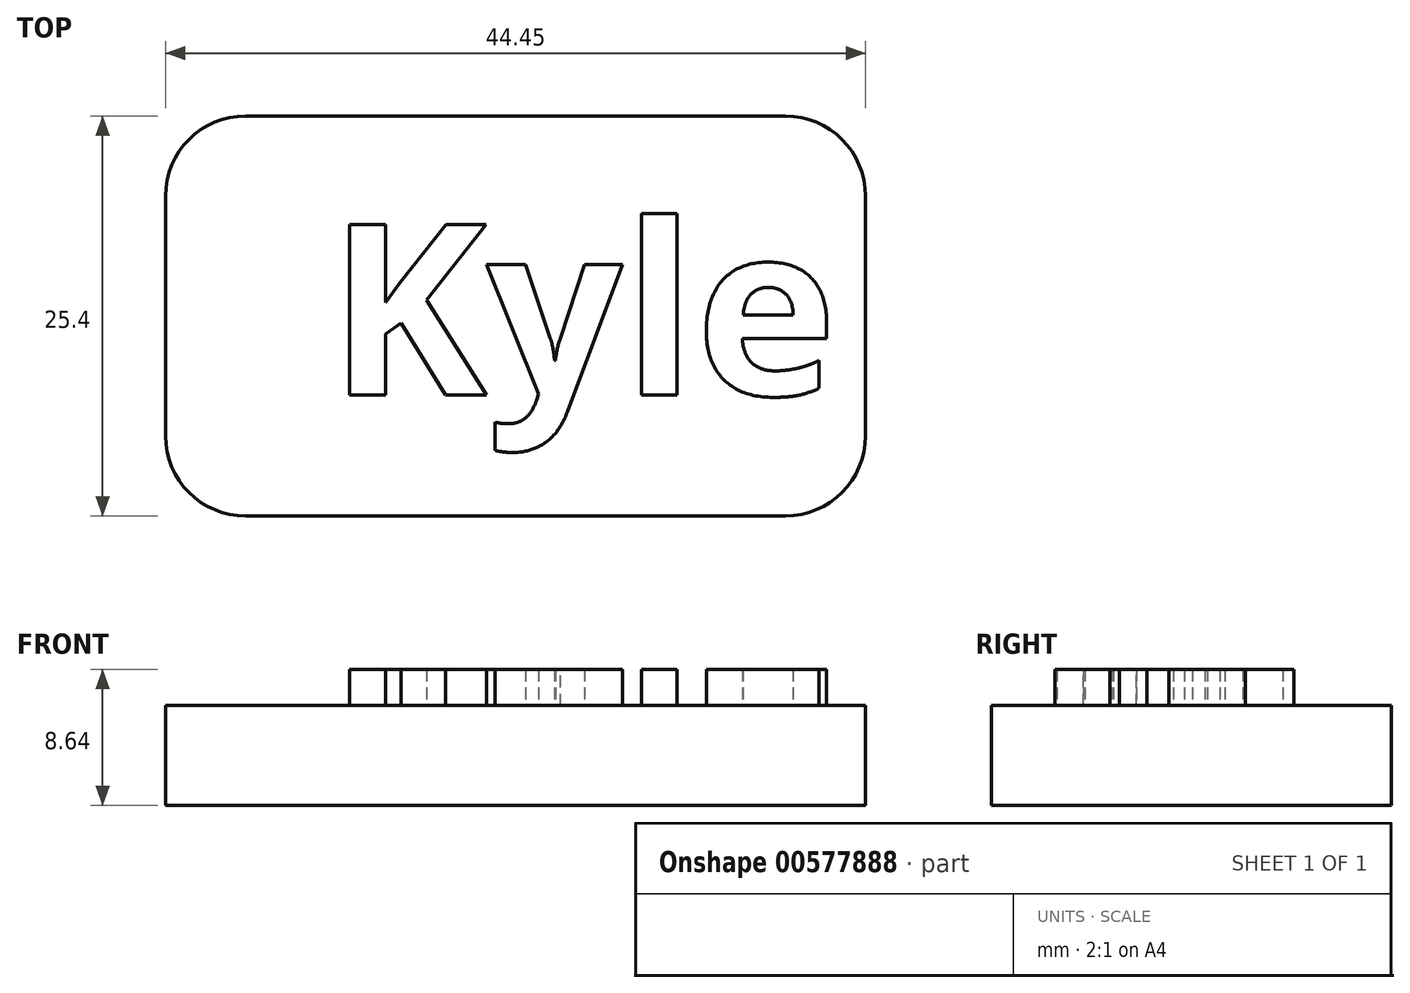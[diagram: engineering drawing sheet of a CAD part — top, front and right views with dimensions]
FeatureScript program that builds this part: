
annotation { "Feature Type Name" : "Feature", "Feature Type Description" : "" }
export const myFeature = defineFeature(function(context is Context, id is Id, definition is map)
    precondition{}
    {
        {
            var Q0;
            Q0=qCreatedBy(makeId("Top.planeOp"),FACE);
            var sketch = newSketch(context, id + "F0", { "sketchPlane" : qUnion([Q0])});
            skLineSegment(sketch, "E0.bottom", {"start": v(-63.11, 52.38) * mm, "end": v(-18.66, 52.38) * mm});
            skLineSegment(sketch, "E0.top", {"start": v(-63.11, 26.98) * mm, "end": v(-18.66, 26.98) * mm});
            skLineSegment(sketch, "E0.left", {"start": v(-63.11, 52.38) * mm, "end": v(-63.11, 26.98) * mm});
            skLineSegment(sketch, "E0.right", {"start": v(-18.66, 52.38) * mm, "end": v(-18.66, 26.98) * mm});
            skSolve(sketch);
        }
        {
            var Q0;
            Q0=makeQuery(id+"F0.imprint","IMPRINT",FACE,{"disambiguationData":[TD([[makeQuery(id+"F0.imprint","IMPRINT",EDGE,{"derivedFrom":sQuery(id+"F0.wireOp",EDGE,"E0.bottom")}),-1.0]])]});
            extrude(context, id + "F1", {"entities" : qUnion([Q0]), "depth" : 6.35 * mm, "offsetDistance" : 25.4 * mm});
        }
        {
            var Q0;
            Q0=makeQuery(id+"F1.opExtrude","CAP_FACE",FACE,{"disambiguationData":[OSD([sQuery(id+"F0.wireOp",EDGE,"E0.bottom"),sQuery(id+"F0.wireOp",EDGE,"E0.top"),sQuery(id+"F0.wireOp",EDGE,"E0.left"),sQuery(id+"F0.wireOp",EDGE,"E0.right")])],"isStart":false});
            var sketch = newSketch(context, id + "F2", { "sketchPlane" : qUnion([Q0])});
            skText(sketch, "E1", { "text": "Kyle", "fontName": "OpenSans-Bold.ttf"});
            const initialGuessF2  = {"E1": [-0.0528, 0.03466, 1, 0, 0.01093]};
            skSetInitialGuess(sketch, initialGuessF2);
            skSolve(sketch);
        }
        {
            var Q0;
            Q0 = qSketchRegion(id + "F2", true);
            extrude(context, id + "F3", {"entities" : qUnion([Q0]), "operationType" : NewBodyOperationType.ADD, "depth" : 2.3 * mm, "offsetDistance" : 25.4 * mm});
        }
        {
            var Q0;
            {var subQ0=sQuery(id+"F0.wireOp",EDGE,"E0.left");var subQ1=sQuery(id+"F0.wireOp",EDGE,"E0.bottom");var subQ2=sQuery(id+"F0.wireOp",EDGE,"E0.right");var subQ3=sQuery(id+"F0.wireOp",EDGE,"E0.top");Q0=makeQuery(id+"F3.boolean.opBoolean","SPLIT",FACE,{"disambiguationData":[TD([makeQuery(id+"F1.opExtrude","SWEPT_FACE",FACE,{"disambiguationData":[OSD([subQ1])]})])],"derivedFrom":makeQuery(id+"F1.opExtrude","CAP_FACE",FACE,{"disambiguationData":[OSD([subQ1,subQ3,subQ0,subQ2])],"isStart":false})});}
            var sketch = newSketch(context, id + "F4", { "sketchPlane" : qUnion([Q0])});
            skCircle(sketch, "E2", {"center": v(-56.75, 39.68) * mm, "radius": 2.84 * mm});
            skPoint(sketch, "E2.centerSnap0", {"position": v(-63.11, 39.68) * mm});
            skSolve(sketch);
        }
        {
            var Q0;
            Q0=sQuery(id+"F4.wireOp",EDGE,"E2");
            extrude(context, id + "F5", {"bodyType" : ToolBodyType.SURFACE, "surfaceEntities" : qUnion([Q0]), "depth" : -6.35 * mm, "offsetDistance" : 25.4 * mm});
        }
        {
            var Q0;
            Q0=makeQuery(id+"F1.opExtrude","SWEPT_EDGE",EDGE,{"disambiguationData":[OSD([sQuery(id+"F0.wireOp",EDGE,"E0.bottom"),sQuery(id+"F0.wireOp",EDGE,"E0.left")])]});
            var Q1;
            Q1=makeQuery(id+"F1.opExtrude","SWEPT_EDGE",EDGE,{"disambiguationData":[OSD([sQuery(id+"F0.wireOp",EDGE,"E0.bottom"),sQuery(id+"F0.wireOp",EDGE,"E0.right")])]});
            var Q2;
            Q2=makeQuery(id+"F1.opExtrude","SWEPT_EDGE",EDGE,{"disambiguationData":[OSD([sQuery(id+"F0.wireOp",EDGE,"E0.top"),sQuery(id+"F0.wireOp",EDGE,"E0.right")])]});
            var Q3;
            Q3=makeQuery(id+"F1.opExtrude","SWEPT_EDGE",EDGE,{"disambiguationData":[OSD([sQuery(id+"F0.wireOp",EDGE,"E0.top"),sQuery(id+"F0.wireOp",EDGE,"E0.left")])]});
            fillet(context, id + "F6", {"entities" : qUnion([Q0, Q1, Q2, Q3]), "radius" : 5.08 * mm, "tangentPropagation" : true, "allowEdgeOverflow" : false});
        }
    });
